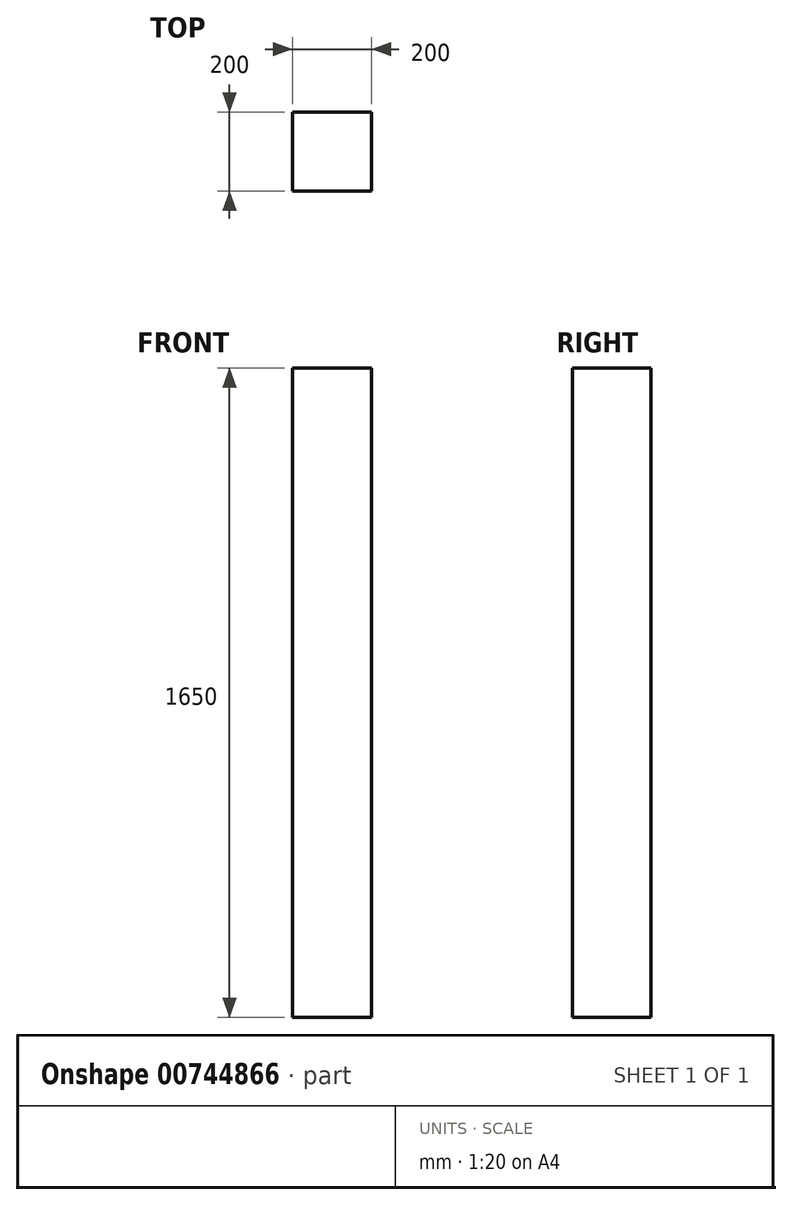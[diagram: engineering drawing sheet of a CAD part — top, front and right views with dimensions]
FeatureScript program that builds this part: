
annotation { "Feature Type Name" : "Feature", "Feature Type Description" : "" }
export const myFeature = defineFeature(function(context is Context, id is Id, definition is map)
    precondition{}
    {
        {
            var Q0;
            Q0=qCreatedBy(makeId("Top.planeOp"),FACE);
            var sketch = newSketch(context, id + "F0", { "sketchPlane" : qUnion([Q0])});
            skLineSegment(sketch, "E0.bottom", {"start": v(0, 0) * mm, "end": v(200, 0) * mm});
            skLineSegment(sketch, "E0.top", {"start": v(0, -200) * mm, "end": v(200, -200) * mm});
            skLineSegment(sketch, "E0.left", {"start": v(0, 0) * mm, "end": v(0, -200) * mm});
            skLineSegment(sketch, "E0.right", {"start": v(200, 0) * mm, "end": v(200, -200) * mm});
            skSolve(sketch);
        }
        {
            var Q0;
            Q0=makeQuery(id+"F0.imprint","IMPRINT",FACE,{"disambiguationData":[TD([[makeQuery(id+"F0.imprint","IMPRINT",EDGE,{"derivedFrom":sQuery(id+"F0.wireOp",EDGE,"E0.bottom")}),-1.0]])]});
            extrude(context, id + "F1", {"entities" : qUnion([Q0]), "flatOperationType" : FlatOperationType.REMOVE, "depth" : 1650 * mm, "offsetDistance" : 25 * mm, "domain" : OperationDomain.MODEL});
        }
    });
